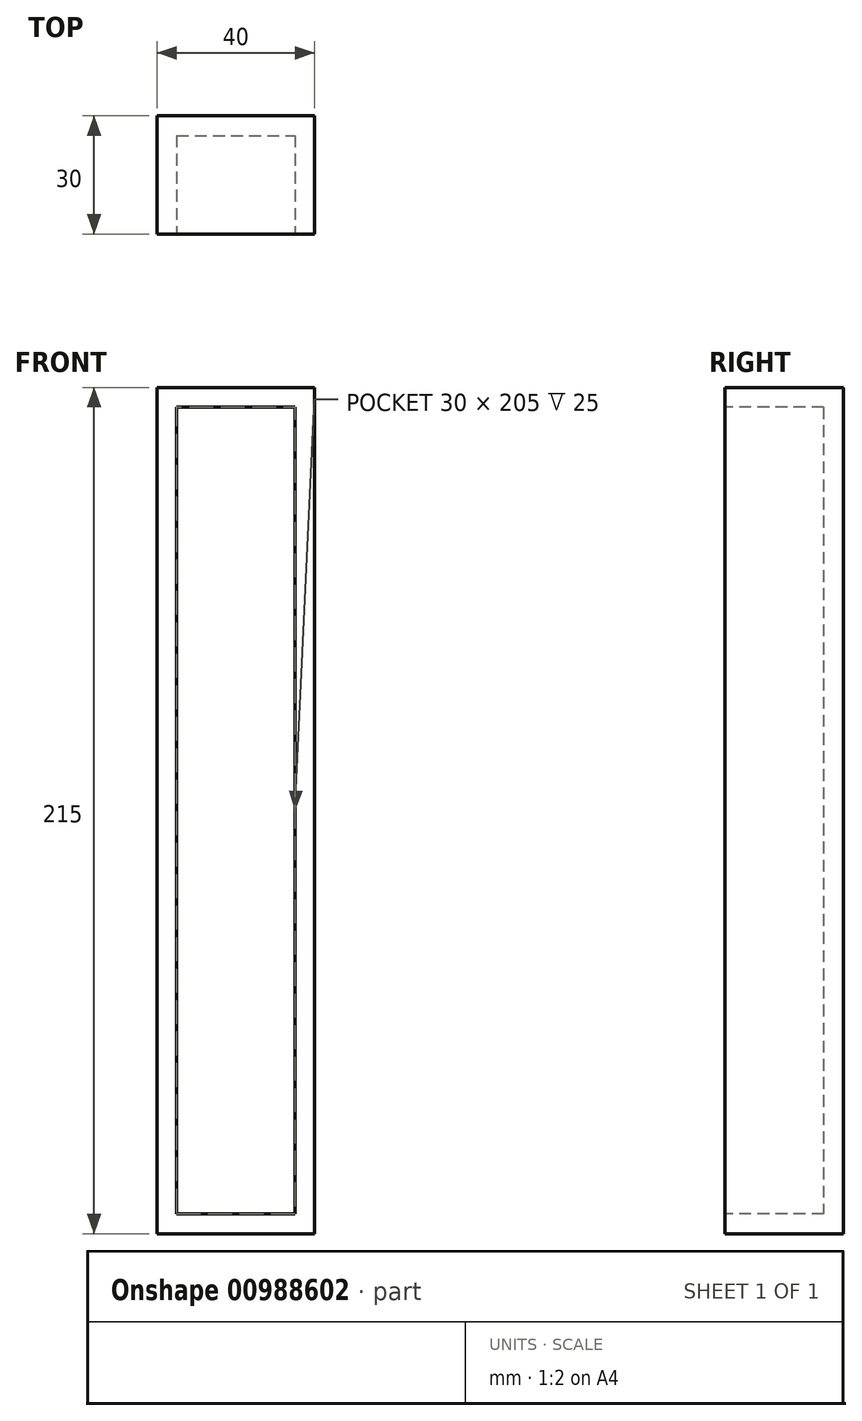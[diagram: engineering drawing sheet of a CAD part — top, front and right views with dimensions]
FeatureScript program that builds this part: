
annotation { "Feature Type Name" : "Feature", "Feature Type Description" : "" }
export const myFeature = defineFeature(function(context is Context, id is Id, definition is map)
    precondition{}
    {
        {
            var Q0;
            Q0=qCreatedBy(makeId("Front.planeOp"),FACE);
            var sketch = newSketch(context, id + "F0", { "sketchPlane" : qUnion([Q0])});
            skLineSegment(sketch, "E0.bottom", {"start": v(-20, 107.5) * mm, "end": v(20, 107.5) * mm});
            skLineSegment(sketch, "E0.top", {"start": v(-20, -107.5) * mm, "end": v(20, -107.5) * mm});
            skLineSegment(sketch, "E0.left", {"start": v(-20, 107.5) * mm, "end": v(-20, -107.5) * mm});
            skLineSegment(sketch, "E0.right", {"start": v(20, 107.5) * mm, "end": v(20, -107.5) * mm});
            skLineSegment(sketch, "E1", {"start": v(-20, 107.5) * mm, "end": v(20, -107.5) * mm, "construction": true});
            skSolve(sketch);
        }
        {
            var Q0;
            Q0 = qSketchRegion(id + "F0", true);
            extrude(context, id + "F1", {"entities" : qUnion([Q0]), "endBound" : BoundingType.SYMMETRIC, "depth" : 30 * mm, "offsetDistance" : 25 * mm});
        }
        {
            var Q0;
            Q0=makeQuery(id+"F1.opExtrude","CAP_FACE",FACE,{"disambiguationData":[OSD([sQuery(id+"F0.wireOp",EDGE,"E0.bottom"),sQuery(id+"F0.wireOp",EDGE,"E0.top"),sQuery(id+"F0.wireOp",EDGE,"E0.left"),sQuery(id+"F0.wireOp",EDGE,"E0.right")])],"isStart":false});
            var sketch = newSketch(context, id + "F2", { "sketchPlane" : qUnion([Q0])});
            skLineSegment(sketch, "E2.0", {"start": v(-15, 102.5) * mm, "end": v(15, 102.5) * mm});
            skLineSegment(sketch, "E2.1", {"start": v(-15, 102.5) * mm, "end": v(-15, -102.5) * mm});
            skLineSegment(sketch, "E2.2", {"start": v(-15, -102.5) * mm, "end": v(15, -102.5) * mm});
            skLineSegment(sketch, "E2.3", {"start": v(15, 102.5) * mm, "end": v(15, -102.5) * mm});
            skSolve(sketch);
        }
        {
            var Q0;
            Q0 = qSketchRegion(id + "F2", true);
            extrude(context, id + "F3", {"entities" : qUnion([Q0]), "operationType" : NewBodyOperationType.REMOVE, "oppositeDirection" : true, "depth" : 25 * mm, "offsetDistance" : 25 * mm});
        }
    });
